# Revit family: P200921MX-076c_MZF34X20DW
name_source: partatom
category: Specialty Equipment
units: mm (PartAtom-declared; Revit-internal decimal feet)

## family parameters
Always vertical = Yes
Cut with Voids When Loaded = No
Enable Cutting in Views = No
Maintain Annotation Orientation = No
Part Type = Normal
Room Calculation Point = No
Round Connector Dimension = Use Diameter
Shared = No
Work Plane-Based = No

## types (1)
- MZF34X20DW
    Accent Material = ARCAT - Metal - Steel - White
    Amps = 0 A
    Body Material = ARCAT - Metal - Steel - White
    Clearance Material = ARCAT - Clearance
    Default Elevation = 0"
    Depth = 29 1/8"
    Description = "20 cu. ft. Frost Free Upright Freezer with LED Lighting
Congélateur vertical sans givre avec éclairage à DEL, 20 pi³"
    Dimension Guide = "http://access.whirlpool.com Guide&sku=MZF34X20DW&language=EN
http://access.whirlpool.com Guide&sku=MZF34X20DW&language=EN"
    Door Material = ARCAT - Metal - Steel - White
    Energy Guide = "http://access.whirlpool.com Guide&sku=MZF34X20DW&language=EN
http://access.whirlpool.com Guide&sku=MZF34X20DW&language=FR"
    Family Name = Refrigeration
    Feature 1 = "10-Year Limited Parts Warranty on the Compressor
Garantie limitée de 10 ans sur les pièces du compresseur*"
    Feature 2 = "LED Lighting
Éclairage à DEL"
    Feature 3 = "Frost Free
Sans givre"
    Height = 66 3/4"
    Manufacturer = Maytag
    Model = MZF34X20DW
    Voltage = 0 V
    Width = 33 1/4"

## geometry (parser evidence)
native form markers: Sweep x4
no freeform markers — native parametric forms only
